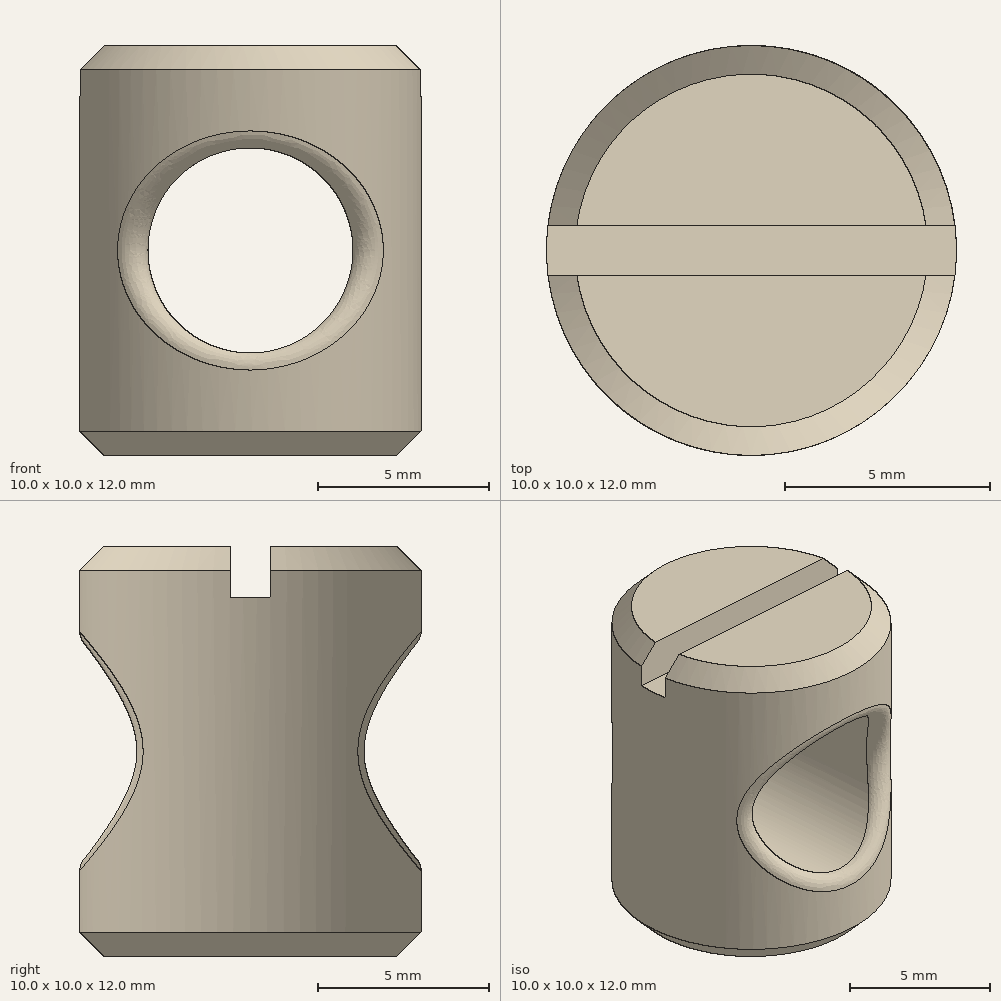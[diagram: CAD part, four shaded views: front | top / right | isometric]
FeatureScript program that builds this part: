
annotation { "Feature Type Name" : "Feature", "Feature Type Description" : "" }
export const myFeature = defineFeature(function(context is Context, id is Id, definition is map)
    precondition{}
    {
        {
            var Q0;
            Q0=qCreatedBy(makeId("Top.planeOp"),FACE);
            var sketch = newSketch(context, id + "F0", { "sketchPlane" : qUnion([Q0])});
            skCircle(sketch, "E0", {"center": v(0, 0) * mm, "radius": 5 * mm});
            skSolve(sketch);
        }
        {
            var Q0;
            Q0 = qSketchRegion(id + "F0", true);
            extrude(context, id + "F1", {"entities" : qUnion([Q0]), "depth" : 12 * mm, "offsetDistance" : 25 * mm});
        }
        {
            var Q0;
            Q0=qCreatedBy(makeId("Front.planeOp"),FACE);
            var sketch = newSketch(context, id + "F2", { "sketchPlane" : qUnion([Q0])});
            skCircle(sketch, "E1", {"center": v(0, 6) * mm, "radius": 3 * mm});
            skSolve(sketch);
        }
        {
            var Q0;
            Q0 = qSketchRegion(id + "F2", true);
            extrude(context, id + "F3", {"entities" : qUnion([Q0]), "operationType" : NewBodyOperationType.REMOVE, "endBound" : BoundingType.SYMMETRIC, "oppositeDirection" : true, "depth" : 25 * mm, "offsetDistance" : 25 * mm});
        }
        {
            var Q0;
            Q0=makeQuery(id+"F1.opExtrude","CAP_FACE",FACE,{"disambiguationData":[OSD([sQuery(id+"F0.wireOp",EDGE,"E0")])],"isStart":false});
            var sketch = newSketch(context, id + "F4", { "sketchPlane" : qUnion([Q0])});
            skLineSegment(sketch, "E2.bottom", {"start": v(-5.87, 0.6) * mm, "end": v(5.87, 0.6) * mm});
            skLineSegment(sketch, "E2.top", {"start": v(-5.87, -0.6) * mm, "end": v(5.87, -0.6) * mm});
            skLineSegment(sketch, "E2.left", {"start": v(-5.87, 0.6) * mm, "end": v(-5.87, -0.6) * mm});
            skLineSegment(sketch, "E2.right", {"start": v(5.87, 0.6) * mm, "end": v(5.87, -0.6) * mm});
            skLineSegment(sketch, "E3", {"start": v(-5.87, 0) * mm, "end": v(0, 0) * mm, "construction": true});
            skLineSegment(sketch, "E4", {"start": v(0, 0) * mm, "end": v(0, 0.6) * mm, "construction": true});
            skPoint(sketch, "E4.endSnap0", {"position": v(0, 0.6) * mm});
            skSolve(sketch);
        }
        {
            var Q0;
            Q0 = qSketchRegion(id + "F4", true);
            extrude(context, id + "F5", {"entities" : qUnion([Q0]), "operationType" : NewBodyOperationType.REMOVE, "oppositeDirection" : true, "depth" : 1.5 * mm, "offsetDistance" : 25 * mm});
        }
        {
            var Q0;
            {var subQ0=sQuery(id+"F0.wireOp",EDGE,"E0");Q0=makeQuery(id+"F5.boolean.opBoolean","SPLIT",EDGE,{"disambiguationData":[TD([makeQuery(id+"F5.opExtrude","SWEPT_FACE",FACE,{"disambiguationData":[OSD([sQuery(id+"F4.wireOp",EDGE,"E2.top")])]})])],"derivedFrom":makeQuery(id+"F1.opExtrude","CAP_EDGE",EDGE,{"disambiguationData":[OSD([subQ0])],"isStart":false})});}
            var Q1;
            {var subQ0=sQuery(id+"F0.wireOp",EDGE,"E0");Q1=makeQuery(id+"F5.boolean.opBoolean","SPLIT",EDGE,{"disambiguationData":[TD([makeQuery(id+"F5.opExtrude","SWEPT_FACE",FACE,{"disambiguationData":[OSD([sQuery(id+"F4.wireOp",EDGE,"E2.bottom")])]})])],"derivedFrom":makeQuery(id+"F1.opExtrude","CAP_EDGE",EDGE,{"disambiguationData":[OSD([subQ0])],"isStart":false})});}
            var Q2;
            Q2=makeQuery(id+"F1.opExtrude","CAP_EDGE",EDGE,{"disambiguationData":[OSD([sQuery(id+"F0.wireOp",EDGE,"E0")])],"isStart":true});
            chamfer(context, id + "F6", {"entities" : qUnion([Q0, Q1, Q2]), "width" : 0.7 * mm, "tangentPropagation" : true});
        }
        {
            var Q0;
            Q0=makeQuery(id+"F3.boolean.opBoolean","COPY",FACE,{"derivedFrom":makeQuery(id+"F3.opExtrude","SWEPT_FACE",FACE,{"disambiguationData":[OSD([sQuery(id+"F2.wireOp",EDGE,"E1")])]})});
            fillet(context, id + "F7", {"entities" : qUnion([Q0]), "radius" : .5 * mm, "tangentPropagation" : true, "allowEdgeOverflow" : false});
        }
    });
